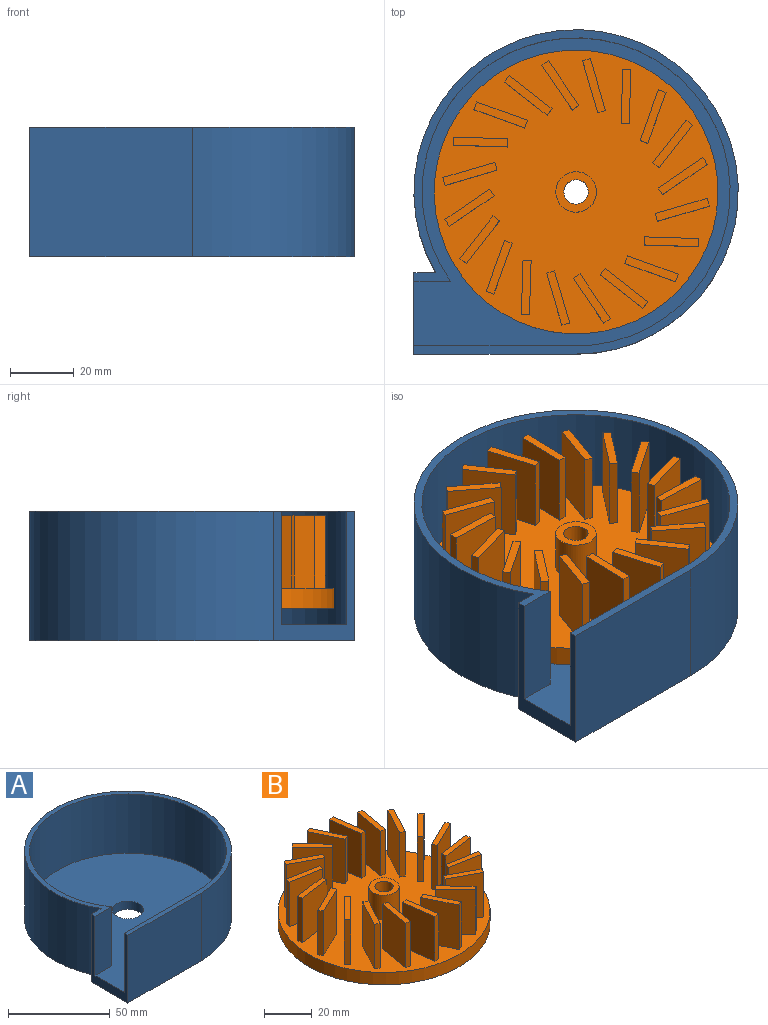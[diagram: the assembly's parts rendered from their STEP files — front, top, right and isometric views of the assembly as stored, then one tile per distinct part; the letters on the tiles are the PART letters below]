
ASSEMBLY  parts=2 mates=1
PART A: 11 faces, bbox 101.6x101.6x40.6 mm
  f0: plane 99.06x96.52mm, normal (0,0,1), area 7606.2mm2, adj f1,f5,f7,f8,f9
  f1: plane 40.64x25.4mm, normal (-1,0,0), area 309.7mm2, adj f0,f2,f4,f6,f8,f9,f10
  f2: plane 50.8x40.64mm, normal (0,-1,0), area 2064.5mm2, adj f1,f3,f6,f10
  f3: cylinder r=50.8mm len=101.6mm, axis (0,0,1), area 10809.8mm2, adj f2,f4,f6,f10
  f4: plane 40.64x6.81mm, normal (0,1,0), area 276.6mm2, adj f1,f3,f6,f10
  f5: cylinder r=7.62mm len=15.24mm, axis (0,0,1), area 243.2mm2, adj f0,f6
  f6: plane 101.6x101.6mm, normal (0,0,-1), area 8422.7mm2, adj f1,f2,f3,f4,f5
  f7: cylinder r=48.26mm len=96.52mm, axis (0,0,-1), area 9146.7mm2, adj f0,f8,f9,f10
  f8: plane 50.8x35.56mm, normal (0,1,0), area 1806.4mm2, adj f0,f1,f7,f10
  f9: plane 35.56x11.45mm, normal (0,-1,0), area 407.2mm2, adj f0,f1,f7,f10
  f10: plane 101.6x101.6mm, normal (0,0,1), area 816.5mm2, adj f1,f2,f3,f4,f7,f8,f9
PART B: 106 faces, bbox 88.9x88.9x29.2 mm
  f0: plane 88.9x88.9mm, normal (0,0,1), area 5220.6mm2, adj f2,f4,f5,f6,f7,f10,f11,f12
  f1: cylinder r=3.81mm len=19.05mm, axis (0,0,-1), area 456mm2, adj f3,f105
  f2: cylinder r=44.45mm len=88.9mm, axis (0,0,-1), area 1773.5mm2, adj f0,f3
  f3: plane 88.9x88.9mm, normal (0,0,-1), area 6161.6mm2, adj f1,f2
  f4: plane 22.86x2.29mm, normal (0.44,-0.9,0), area 58.1mm2, adj f0,f5,f7,f8
  f5: plane 22.86x15.24mm, normal (0.9,0.44,0), area 387mm2, adj f0,f4,f6,f8
  f6: plane 22.86x2.29mm, normal (-0.44,0.9,0), area 58.1mm2, adj f0,f5,f7,f8
  f7: plane 22.86x15.24mm, normal (-0.9,-0.44,0), area 387mm2, adj f0,f4,f6,f8
  f8: plane 16.35x9.65mm, normal (0,0,1), area 43mm2, adj f4,f5,f6,f7
  f9: plane 17.11x5.5mm, normal (0,0,1), area 43mm2, adj f10,f11,f12,f13
  f10: plane 22.86x16.66mm, normal (-0.98,0.18,0), area 387mm2, adj f0,f9,f11,f13
  f11: plane 22.86x2.5mm, normal (0.18,0.98,0), area 58.1mm2, adj f0,f9,f10,f12
  f12: plane 22.86x16.66mm, normal (0.98,-0.18,0), area 387mm2, adj f0,f9,f11,f13
  f13: plane 22.86x2.5mm, normal (-0.18,-0.98,0), area 58.1mm2, adj f0,f9,f10,f12
  f14: plane 13.98x13.55mm, normal (0,0,1), area 43mm2, adj f15,f16,f17,f18
  f15: plane 22.86x12.22mm, normal (-0.69,0.72,0), area 387mm2, adj f0,f14,f16,f18
  f16: plane 22.86x1.83mm, normal (0.72,0.69,0), area 58.1mm2, adj f0,f14,f15,f17
  f17: plane 22.86x12.22mm, normal (0.69,-0.72,0), area 387mm2, adj f0,f14,f16,f18
  f18: plane 22.86x1.83mm, normal (-0.72,-0.69,0), area 58.1mm2, adj f0,f14,f15,f17
  f19: plane 17.12x4.81mm, normal (0,0,1), area 43mm2, adj f20,f21,f22,f23
  f20: plane 22.86x16.77mm, normal (-0.14,0.99,0), area 387mm2, adj f0,f19,f21,f23
  f21: plane 22.86x2.52mm, normal (0.99,0.14,0), area 58.1mm2, adj f0,f19,f20,f22
  f22: plane 22.86x16.77mm, normal (0.14,-0.99,0), area 387mm2, adj f0,f19,f21,f23
  f23: plane 22.86x2.52mm, normal (-0.99,-0.14,0), area 58.1mm2, adj f0,f19,f20,f22
  f24: plane 16.12x10.24mm, normal (0,0,1), area 43mm2, adj f25,f26,f27,f28
  f25: plane 22.86x14.92mm, normal (0.47,0.88,0), area 387mm2, adj f0,f24,f26,f28
  f26: plane 22.86x2.24mm, normal (0.88,-0.47,0), area 58.1mm2, adj f0,f24,f25,f27
  f27: plane 22.86x14.92mm, normal (-0.47,-0.88,0), area 387mm2, adj f0,f24,f26,f28
  f28: plane 22.86x2.24mm, normal (-0.88,0.47,0), area 58.1mm2, adj f0,f24,f25,f27
  f29: plane 16.35x9.65mm, normal (0,0,1), area 43mm2, adj f30,f31,f32,f33
  f30: plane 22.86x15.24mm, normal (0.9,0.44,0), area 387mm2, adj f0,f29,f31,f33
  f31: plane 22.86x2.29mm, normal (0.44,-0.9,0), area 58.1mm2, adj f0,f29,f30,f32
  f32: plane 22.86x15.24mm, normal (-0.9,-0.44,0), area 387mm2, adj f0,f29,f31,f33
  f33: plane 22.86x2.29mm, normal (-0.44,0.9,0), area 58.1mm2, adj f0,f29,f30,f32
  f34: plane 17.11x5.5mm, normal (0,0,1), area 43mm2, adj f35,f36,f37,f38
  f35: plane 22.86x16.66mm, normal (0.98,-0.18,0), area 387mm2, adj f0,f34,f36,f38
  f36: plane 22.86x2.5mm, normal (-0.18,-0.98,0), area 58.1mm2, adj f0,f34,f35,f37
  f37: plane 22.86x16.66mm, normal (-0.98,0.18,0), area 387mm2, adj f0,f34,f36,f38
  f38: plane 22.86x2.5mm, normal (0.18,0.98,0), area 58.1mm2, adj f0,f34,f35,f37
  f39: plane 13.98x13.55mm, normal (0,0,1), area 43mm2, adj f40,f41,f42,f43
  f40: plane 22.86x12.22mm, normal (0.69,-0.72,0), area 387mm2, adj f0,f39,f41,f43
  f41: plane 22.86x1.83mm, normal (-0.72,-0.69,0), area 58.1mm2, adj f0,f39,f40,f42
  f42: plane 22.86x12.22mm, normal (-0.69,0.72,0), area 387mm2, adj f0,f39,f41,f43
  f43: plane 22.86x1.83mm, normal (0.72,0.69,0), area 58.1mm2, adj f0,f39,f40,f42
  f44: plane 17.12x4.81mm, normal (0,0,1), area 43mm2, adj f45,f46,f47,f48
  f45: plane 22.86x16.77mm, normal (0.14,-0.99,0), area 387mm2, adj f0,f44,f46,f48
  f46: plane 22.86x2.52mm, normal (-0.99,-0.14,0), area 58.1mm2, adj f0,f44,f45,f47
  f47: plane 22.86x16.77mm, normal (-0.14,0.99,0), area 387mm2, adj f0,f44,f46,f48
  f48: plane 22.86x2.52mm, normal (0.99,0.14,0), area 58.1mm2, adj f0,f44,f45,f47
  f49: plane 16.12x10.24mm, normal (0,0,1), area 43mm2, adj f50,f51,f52,f53
  f50: plane 22.86x14.92mm, normal (-0.47,-0.88,0), area 387mm2, adj f0,f49,f51,f53
  f51: plane 22.86x2.24mm, normal (-0.88,0.47,0), area 58.1mm2, adj f0,f49,f50,f52
  f52: plane 22.86x14.92mm, normal (0.47,0.88,0), area 387mm2, adj f0,f49,f51,f53
  f53: plane 22.86x2.24mm, normal (0.88,-0.47,0), area 58.1mm2, adj f0,f49,f50,f52
  f54: plane 13.98x13.55mm, normal (0,0,1), area 43mm2, adj f55,f56,f57,f58
  f55: plane 22.86x1.83mm, normal (0.69,-0.72,0), area 58.1mm2, adj f0,f54,f56,f58
  f56: plane 22.86x12.22mm, normal (0.72,0.69,0), area 387mm2, adj f0,f54,f55,f57
  f57: plane 22.86x1.83mm, normal (-0.69,0.72,0), area 58.1mm2, adj f0,f54,f56,f58
  f58: plane 22.86x12.22mm, normal (-0.72,-0.69,0), area 387mm2, adj f0,f54,f55,f57
  f59: plane 17.11x5.5mm, normal (0,0,1), area 43mm2, adj f60,f61,f62,f63
  f60: plane 22.86x2.5mm, normal (0.98,-0.18,0), area 58.1mm2, adj f0,f59,f61,f63
  f61: plane 22.86x16.66mm, normal (0.18,0.98,0), area 387mm2, adj f0,f59,f60,f62
  f62: plane 22.86x2.5mm, normal (-0.98,0.18,0), area 58.1mm2, adj f0,f59,f61,f63
  f63: plane 22.86x16.66mm, normal (-0.18,-0.98,0), area 387mm2, adj f0,f59,f60,f62
  f64: plane 16.35x9.65mm, normal (0,0,1), area 43mm2, adj f65,f66,f67,f68
  f65: plane 22.86x2.29mm, normal (0.9,0.44,0), area 58.1mm2, adj f0,f64,f66,f68
  f66: plane 22.86x15.24mm, normal (-0.44,0.9,0), area 387mm2, adj f0,f64,f65,f67
  f67: plane 22.86x2.29mm, normal (-0.9,-0.44,0), area 58.1mm2, adj f0,f64,f66,f68
  f68: plane 22.86x15.24mm, normal (0.44,-0.9,0), area 387mm2, adj f0,f64,f65,f67
  f69: plane 16.12x10.24mm, normal (0,0,1), area 43mm2, adj f70,f71,f72,f73
  f70: plane 22.86x2.24mm, normal (0.47,0.88,0), area 58.1mm2, adj f0,f69,f71,f73
  f71: plane 22.86x14.92mm, normal (-0.88,0.47,0), area 387mm2, adj f0,f69,f70,f72
  f72: plane 22.86x2.24mm, normal (-0.47,-0.88,0), area 58.1mm2, adj f0,f69,f71,f73
  f73: plane 22.86x14.92mm, normal (0.88,-0.47,0), area 387mm2, adj f0,f69,f70,f72
  f74: plane 17.12x4.81mm, normal (0,0,1), area 43mm2, adj f75,f76,f77,f78
  f75: plane 22.86x2.52mm, normal (-0.14,0.99,0), area 58.1mm2, adj f0,f74,f76,f78
  f76: plane 22.86x16.77mm, normal (-0.99,-0.14,0), area 387mm2, adj f0,f74,f75,f77
  f77: plane 22.86x2.52mm, normal (0.14,-0.99,0), area 58.1mm2, adj f0,f74,f76,f78
  f78: plane 22.86x16.77mm, normal (0.99,0.14,0), area 387mm2, adj f0,f74,f75,f77
  f79: plane 13.98x13.55mm, normal (0,0,1), area 43mm2, adj f80,f81,f82,f83
  f80: plane 22.86x1.83mm, normal (-0.69,0.72,0), area 58.1mm2, adj f0,f79,f81,f83
  f81: plane 22.86x12.22mm, normal (-0.72,-0.69,0), area 387mm2, adj f0,f79,f80,f82
  f82: plane 22.86x1.83mm, normal (0.69,-0.72,0), area 58.1mm2, adj f0,f79,f81,f83
  f83: plane 22.86x12.22mm, normal (0.72,0.69,0), area 387mm2, adj f0,f79,f80,f82
  f84: plane 17.11x5.5mm, normal (0,0,1), area 43mm2, adj f85,f86,f87,f88
  f85: plane 22.86x2.5mm, normal (-0.98,0.18,0), area 58.1mm2, adj f0,f84,f86,f88
  f86: plane 22.86x16.66mm, normal (-0.18,-0.98,0), area 387mm2, adj f0,f84,f85,f87
  f87: plane 22.86x2.5mm, normal (0.98,-0.18,0), area 58.1mm2, adj f0,f84,f86,f88
  f88: plane 22.86x16.66mm, normal (0.18,0.98,0), area 387mm2, adj f0,f84,f85,f87
  f89: plane 16.35x9.65mm, normal (0,0,1), area 43mm2, adj f90,f91,f92,f93
  f90: plane 22.86x2.29mm, normal (-0.9,-0.44,0), area 58.1mm2, adj f0,f89,f91,f93
  f91: plane 22.86x15.24mm, normal (0.44,-0.9,0), area 387mm2, adj f0,f89,f90,f92
  f92: plane 22.86x2.29mm, normal (0.9,0.44,0), area 58.1mm2, adj f0,f89,f91,f93
  f93: plane 22.86x15.24mm, normal (-0.44,0.9,0), area 387mm2, adj f0,f89,f90,f92
  f94: plane 16.12x10.24mm, normal (0,0,1), area 43mm2, adj f95,f96,f97,f98
  f95: plane 22.86x2.24mm, normal (-0.47,-0.88,0), area 58.1mm2, adj f0,f94,f96,f98
  f96: plane 22.86x14.92mm, normal (0.88,-0.47,0), area 387mm2, adj f0,f94,f95,f97
  f97: plane 22.86x2.24mm, normal (0.47,0.88,0), area 58.1mm2, adj f0,f94,f96,f98
  f98: plane 22.86x14.92mm, normal (-0.88,0.47,0), area 387mm2, adj f0,f94,f95,f97
  f99: plane 22.86x2.52mm, normal (0.14,-0.99,0), area 58.1mm2, adj f0,f100,f102,f103
  f100: plane 22.86x16.77mm, normal (0.99,0.14,0), area 387mm2, adj f0,f99,f101,f103
  f101: plane 22.86x2.52mm, normal (-0.14,0.99,0), area 58.1mm2, adj f0,f100,f102,f103
  f102: plane 22.86x16.77mm, normal (-0.99,-0.14,0), area 387mm2, adj f0,f99,f101,f103
  f103: plane 17.12x4.81mm, normal (0,0,1), area 43mm2, adj f99,f100,f101,f102
  f104: cylinder r=6.35mm len=12.7mm, axis (0,0,-1), area 506.7mm2, adj f0,f105
  f105: plane 12.7x12.7mm, normal (0,0,1), area 81.1mm2, adj f1,f104
PLACE A t=(-4.45,-6.11,-20.56)mm fixed
PLACE B rot(axis=(0,0,-1),135.6deg) t=(-4.45,-6.11,-15.48)mm
MATE revolute B.f1 <-> A.f3  axis (0,0,-1) through (-4.45,-6.11,-15.48)mm
